# Revit family: Toilet-Floor_Mount-KOHLER-Family_Care-K-23191K
name_source: partatom
category: Plumbing Fixtures
units: mm (PartAtom-declared; Revit-internal decimal feet)

## family parameters
Cut with Voids When Loaded = No
Host = Face
Maintain Annotation Orientation = No
OmniClass Number = 23.31.19.00
OmniClass Title = Toilets
Part Type = Normal
Room Calculation Point = No
Round Connector Dimension = Use Diameter
Shared = No

## types (2) — shared parameters
ADA Compliant = No
Assembly Code = D2010100
Bowl Height = 15 3/8"
CW Connection = Yes
Cold Water Inlet = Cold Water Inlet
Date Modified = 12/09/2025
Default Elevation = 0"
Description = Two-piece elongated toilet with skirted trapway, dual-flush
Finish = Kohler-Vitreous_China-0-White
Flow Rate = 0 GPM
Flush Rate- GPF = 1.28 GPF
Flush Rate- LPF = 4.8 LPF
HW Connection = No
Height = 31"
Hot Water Inlet = Hot Water Inlet
Length = 27 13/16"
Manufacturer = Kohler Co.
Master Format 2014 = 22 42 13.13
Master Format 2014 Name = Residential Water Closets
Material = Vitreous China
Pressure = 0.00 psi
Product Name = Family Care
Product Page URL = https://www.kohlerasiapacific.com
Rough-In = 12"
URL = https://www.kohlerasiapacific.com
Vent Connection = No
Waste Connection = Yes
Waste Water Outlet = Waste Water Outlet
WaterSense Certified = No
Width = 15 11/16"

## per-type parameters (varying)
| type | Model | Product Documentation Link | Seat Included | Type |
| Without Seat, 0-White | K-23191K-NS-0 | https://techcomm.kohler.com | No | 1 |
| With Seat, 0-White | K-23191K-S-0 |  | Yes | 2 |

## geometry (parser evidence)
native form markers: Sweep x6
no freeform markers — native parametric forms only
